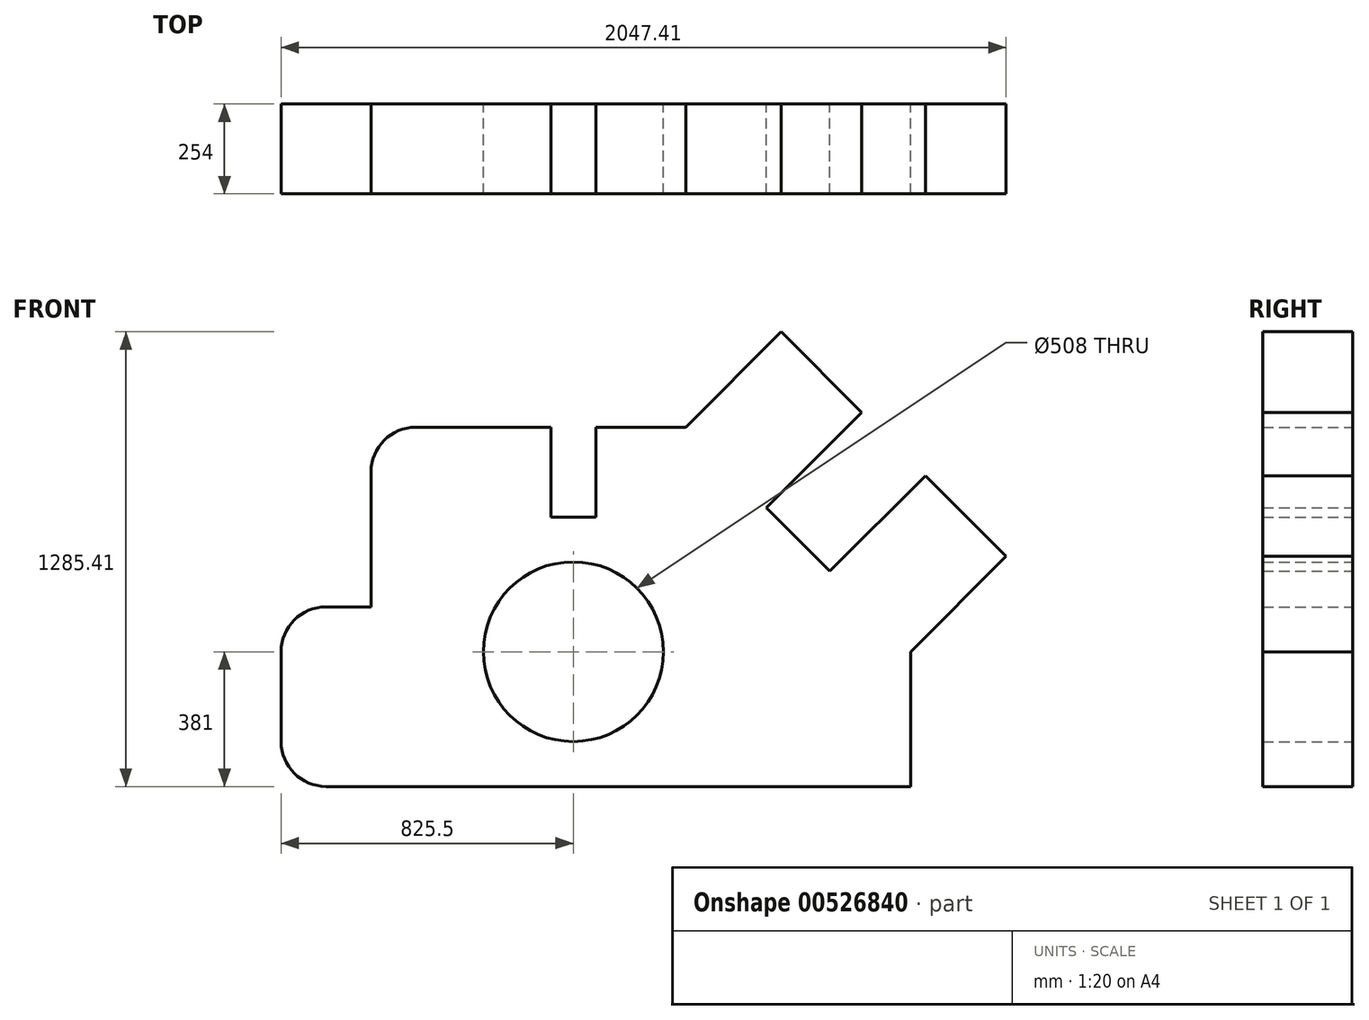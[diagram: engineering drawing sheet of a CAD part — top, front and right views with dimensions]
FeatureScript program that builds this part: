
annotation { "Feature Type Name" : "Feature", "Feature Type Description" : "" }
export const myFeature = defineFeature(function(context is Context, id is Id, definition is map)
    precondition{}
    {
        {
            var Q0;
            Q0=qCreatedBy(makeId("Front.planeOp"),FACE);
            var sketch = newSketch(context, id + "F0", { "sketchPlane" : qUnion([Q0])});
            skLineSegment(sketch, "E0", {"start": v(127, 0) * mm, "end": v(1778, 0) * mm});
            skLineSegment(sketch, "E1", {"start": v(1778, 0) * mm, "end": v(1778, 381) * mm});
            skLineSegment(sketch, "E2", {"start": v(0, 127) * mm, "end": v(0, 381) * mm});
            skPoint(sketch, "E3.visualSharp", {"position": v(0, 0) * mm});
            skArc(sketch, "E3.filletArc", {"start": v(0, 127) * mm, "mid": v(37.2, 37.2) * mm, "end": v(127, 0) * mm});
            skCircle(sketch, "E4", {"center": v(825.5, 381) * mm, "radius": 254 * mm});
            skLineSegment(sketch, "E5", {"start": v(127, 508) * mm, "end": v(254, 508) * mm});
            skLineSegment(sketch, "E6", {"start": v(254, 508) * mm, "end": v(254, 889) * mm});
            skLineSegment(sketch, "E7", {"start": v(381, 1016) * mm, "end": v(762, 1016) * mm});
            skLineSegment(sketch, "E8", {"start": v(762, 1016) * mm, "end": v(762, 762) * mm});
            skLineSegment(sketch, "E9", {"start": v(762, 762) * mm, "end": v(889, 762) * mm});
            skLineSegment(sketch, "E10", {"start": v(889, 762) * mm, "end": v(889, 1016) * mm});
            skLineSegment(sketch, "E11", {"start": v(889, 1016) * mm, "end": v(1143, 1016) * mm});
            skLineSegment(sketch, "E12", {"start": v(1778, 381) * mm, "end": v(2047.4, 650.4) * mm});
            skLineSegment(sketch, "E13", {"start": v(2047.4, 650.4) * mm, "end": v(1819.71, 878.1) * mm});
            skLineSegment(sketch, "E14", {"start": v(1819.71, 878.1) * mm, "end": v(1550.3, 608.7) * mm});
            skLineSegment(sketch, "E15", {"start": v(1550.3, 608.7) * mm, "end": v(1370.7, 788.3) * mm});
            skLineSegment(sketch, "E16", {"start": v(1370.7, 788.3) * mm, "end": v(1640.1, 1057.71) * mm});
            skLineSegment(sketch, "E17", {"start": v(1640.1, 1057.71) * mm, "end": v(1412.4, 1285.4) * mm});
            skLineSegment(sketch, "E18", {"start": v(1412.4, 1285.4) * mm, "end": v(1143, 1016) * mm});
            skPoint(sketch, "E19.visualSharp", {"position": v(0, 508) * mm});
            skArc(sketch, "E19.filletArc", {"start": v(127, 508) * mm, "mid": v(37.2, 470.8) * mm, "end": v(0, 381) * mm});
            skPoint(sketch, "E20.visualSharp", {"position": v(254, 1016) * mm});
            skArc(sketch, "E20.filletArc", {"start": v(381, 1016) * mm, "mid": v(291.2, 978.8) * mm, "end": v(254, 889) * mm});
            skSolve(sketch);
        }
        {
            var Q0;
            Q0 = qSketchRegion(id + "F0", true);
            extrude(context, id + "F1", {"entities" : qUnion([Q0]), "depth" : 254 * mm, "offsetDistance" : 25.4 * mm});
        }
    });
